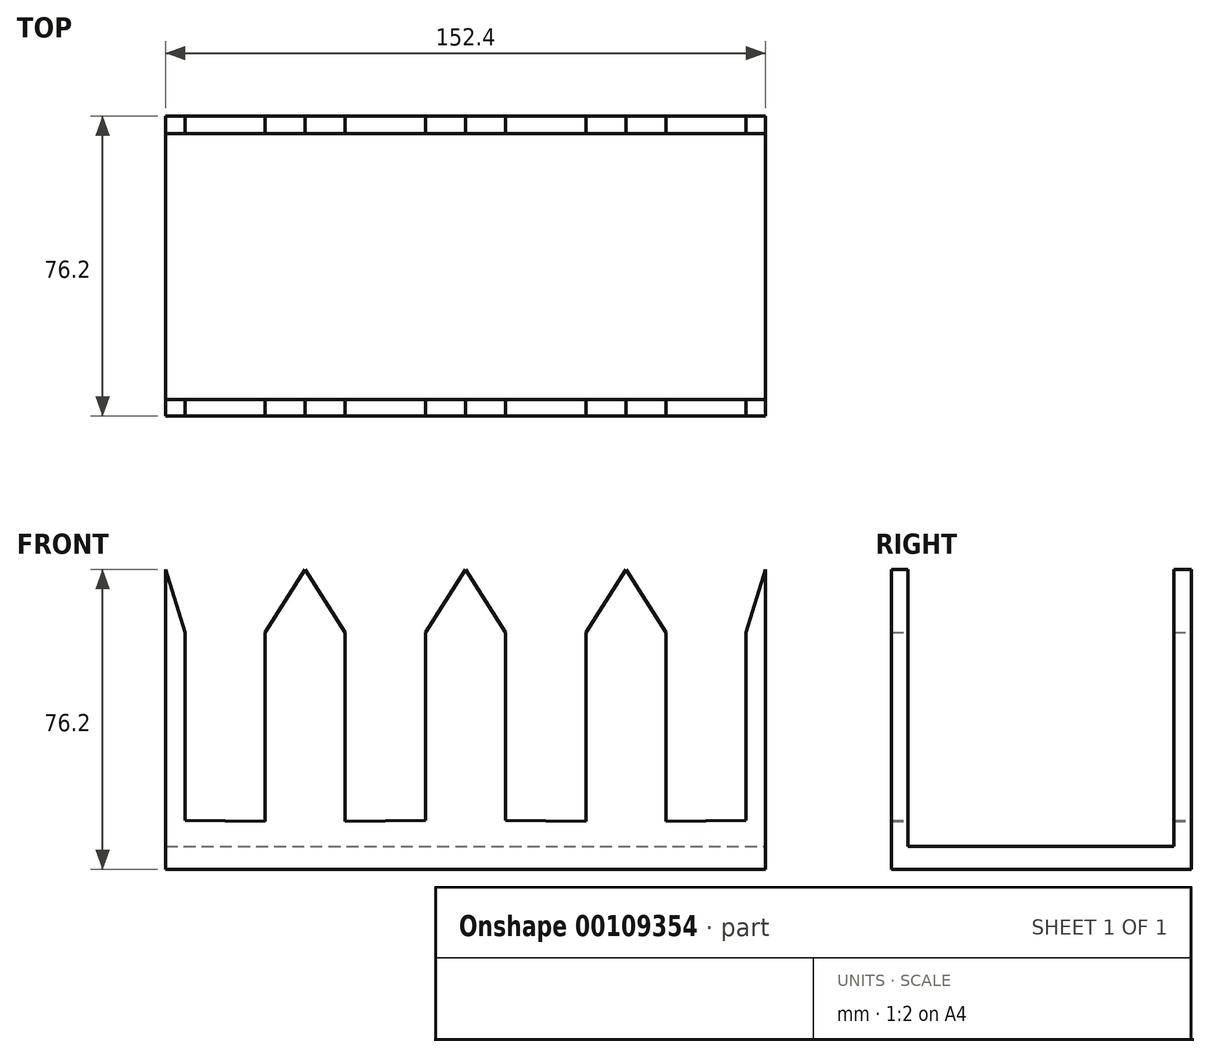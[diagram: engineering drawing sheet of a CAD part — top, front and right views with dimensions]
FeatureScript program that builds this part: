
annotation { "Feature Type Name" : "Feature", "Feature Type Description" : "" }
export const myFeature = defineFeature(function(context is Context, id is Id, definition is map)
    precondition{}
    {
        {
            var Q0;
            Q0=qCreatedBy(makeId("Front.planeOp"),FACE);
            var sketch = newSketch(context, id + "F0", { "sketchPlane" : qUnion([Q0])});
            skLineSegment(sketch, "E0.bottom", {"start": v(0, 0) * mm, "end": v(76.2, 0) * mm});
            skLineSegment(sketch, "E0.left", {"start": v(0, 0) * mm, "end": v(0, 76.2) * mm});
            skLineSegment(sketch, "E0.right", {"start": v(76.2, 0) * mm, "end": v(76.2, 76.2) * mm});
            skLineSegment(sketch, "E1", {"start": v(30.55, 60.27) * mm, "end": v(40.74, 76.2) * mm});
            skLineSegment(sketch, "E2", {"start": v(10.18, 60.27) * mm, "end": v(0, 76.2) * mm});
            skLineSegment(sketch, "E3", {"start": v(10.18, 60.27) * mm, "end": v(10.18, 48.33) * mm});
            skLineSegment(sketch, "E4", {"start": v(30.55, 60.27) * mm, "end": v(30.55, 48.33) * mm});
            skLineSegment(sketch, "E5", {"start": v(10.18, 48.33) * mm, "end": v(10.18, 12.5) * mm});
            skLineSegment(sketch, "E6", {"start": v(30.55, 48.33) * mm, "end": v(30.55, 12.17) * mm});
            skPoint(sketch, "E7.orphan", {"position": v(20.37, 44.33) * mm});
            skPoint(sketch, "E8.start.orphan", {"position": v(0, 44.33) * mm});
            skPoint(sketch, "E9.trimOffspring.end.orphan", {"position": v(40.74, 44.33) * mm});
            skLineSegment(sketch, "E10.MirrorCS", {"start": v(50.92, 60.27) * mm, "end": v(40.74, 76.2) * mm});
            skLineSegment(sketch, "E11.MirrorCS", {"start": v(50.92, 60.27) * mm, "end": v(50.92, 48.33) * mm});
            skLineSegment(sketch, "E12.MirrorCS", {"start": v(50.92, 48.33) * mm, "end": v(50.92, 12.17) * mm});
            skLineSegment(sketch, "E13", {"start": v(10.18, 12.5) * mm, "end": v(30.55, 12.17) * mm});
            skLineSegment(sketch, "E14.MirrorCS", {"start": v(71.29, 12.5) * mm, "end": v(50.92, 12.17) * mm});
            skLineSegment(sketch, "E15.MirrorCS", {"start": v(71.29, 48.33) * mm, "end": v(71.29, 12.5) * mm});
            skLineSegment(sketch, "E16.MirrorCS", {"start": v(71.29, 60.27) * mm, "end": v(71.29, 48.33) * mm});
            skPoint(sketch, "E17.orphan", {"position": v(81.47, 76.2) * mm});
            skPoint(sketch, "E18.MirrorCS.start.orphan", {"position": v(71.29, 60.27) * mm});
            skLineSegment(sketch, "E19", {"start": v(71.29, 60.27) * mm, "end": v(76.2, 76.2) * mm});
            skPoint(sketch, "E20.end.orphan", {"position": v(40.74, 0) * mm});
            skLineSegment(sketch, "E21.MirrorCS", {"start": v(-10.18, 60.27) * mm, "end": v(0, 76.2) * mm});
            skPoint(sketch, "E22.MirrorP", {"position": v(-81.47, 76.2) * mm});
            skPoint(sketch, "E23.MirrorP", {"position": v(-20.37, 44.33) * mm});
            skLineSegment(sketch, "E24.MirrorCS", {"start": v(-71.29, 48.33) * mm, "end": v(-71.29, 12.5) * mm});
            skLineSegment(sketch, "E25.MirrorCS", {"start": v(-71.29, 60.27) * mm, "end": v(-76.2, 76.2) * mm});
            skLineSegment(sketch, "E26.MirrorCS", {"start": v(-71.29, 60.27) * mm, "end": v(-71.29, 48.33) * mm});
            skLineSegment(sketch, "E27.MirrorCS", {"start": v(-71.29, 12.5) * mm, "end": v(-50.92, 12.17) * mm});
            skLineSegment(sketch, "E28.MirrorCS", {"start": v(-50.92, 60.27) * mm, "end": v(-50.92, 48.33) * mm});
            skPoint(sketch, "E29.MirrorP", {"position": v(-40.74, 0) * mm});
            skPoint(sketch, "E30.MirrorP", {"position": v(-71.29, 60.27) * mm});
            skLineSegment(sketch, "E31.MirrorCS", {"start": v(-30.55, 48.33) * mm, "end": v(-30.55, 12.17) * mm});
            skLineSegment(sketch, "E32.MirrorCS", {"start": v(-10.18, 48.33) * mm, "end": v(-10.18, 12.5) * mm});
            skLineSegment(sketch, "E33.MirrorCS", {"start": v(-50.92, 60.27) * mm, "end": v(-40.74, 76.2) * mm});
            skLineSegment(sketch, "E34.MirrorCS", {"start": v(-30.55, 60.27) * mm, "end": v(-30.55, 48.33) * mm});
            skLineSegment(sketch, "E35.MirrorCS", {"start": v(-10.18, 60.27) * mm, "end": v(-10.18, 48.33) * mm});
            skLineSegment(sketch, "E36.MirrorCS", {"start": v(-10.18, 12.5) * mm, "end": v(-30.55, 12.17) * mm});
            skLineSegment(sketch, "E37.MirrorCS", {"start": v(-30.55, 60.27) * mm, "end": v(-40.74, 76.2) * mm});
            skLineSegment(sketch, "E38.MirrorCS", {"start": v(0, 0) * mm, "end": v(-76.2, 0) * mm});
            skPoint(sketch, "E39.MirrorP", {"position": v(-40.74, 44.33) * mm});
            skLineSegment(sketch, "E40.MirrorCS", {"start": v(-50.92, 48.33) * mm, "end": v(-50.92, 12.17) * mm});
            skLineSegment(sketch, "E41.MirrorCS", {"start": v(-76.2, 0) * mm, "end": v(-76.2, 76.2) * mm});
            skSolve(sketch);
        }
        {
            var Q0;
            Q0 = qSketchRegion(id + "F0", true);
            extrude(context, id + "F1", {"entities" : qUnion([Q0]), "depth" : 76.2 * mm});
        }
        {
            var Q0;
            Q0=makeQuery(id+"F1.opExtrude","SWEPT_FACE",FACE,{"disambiguationData":[OSD([sQuery(id+"F0.wireOp",EDGE,"E0.right")])]});
            var sketch = newSketch(context, id + "F2", { "sketchPlane" : qUnion([Q0])});
            skLineSegment(sketch, "E42.bottom", {"start": v(-72.06, 5.84) * mm, "end": v(-4.47, 5.84) * mm});
            skLineSegment(sketch, "E42.top", {"start": v(-72.06, 85.1) * mm, "end": v(-4.47, 85.1) * mm});
            skLineSegment(sketch, "E42.left", {"start": v(-72.06, 5.84) * mm, "end": v(-72.06, 85.1) * mm});
            skLineSegment(sketch, "E42.right", {"start": v(-4.47, 5.84) * mm, "end": v(-4.47, 85.1) * mm});
            skSolve(sketch);
        }
        {
            var Q0;
            Q0 = qSketchRegion(id + "F2", true);
            extrude(context, id + "F3", {"entities" : qUnion([Q0]), "operationType" : NewBodyOperationType.REMOVE, "oppositeDirection" : true, "depth" : 177.8 * mm});
        }
    });
